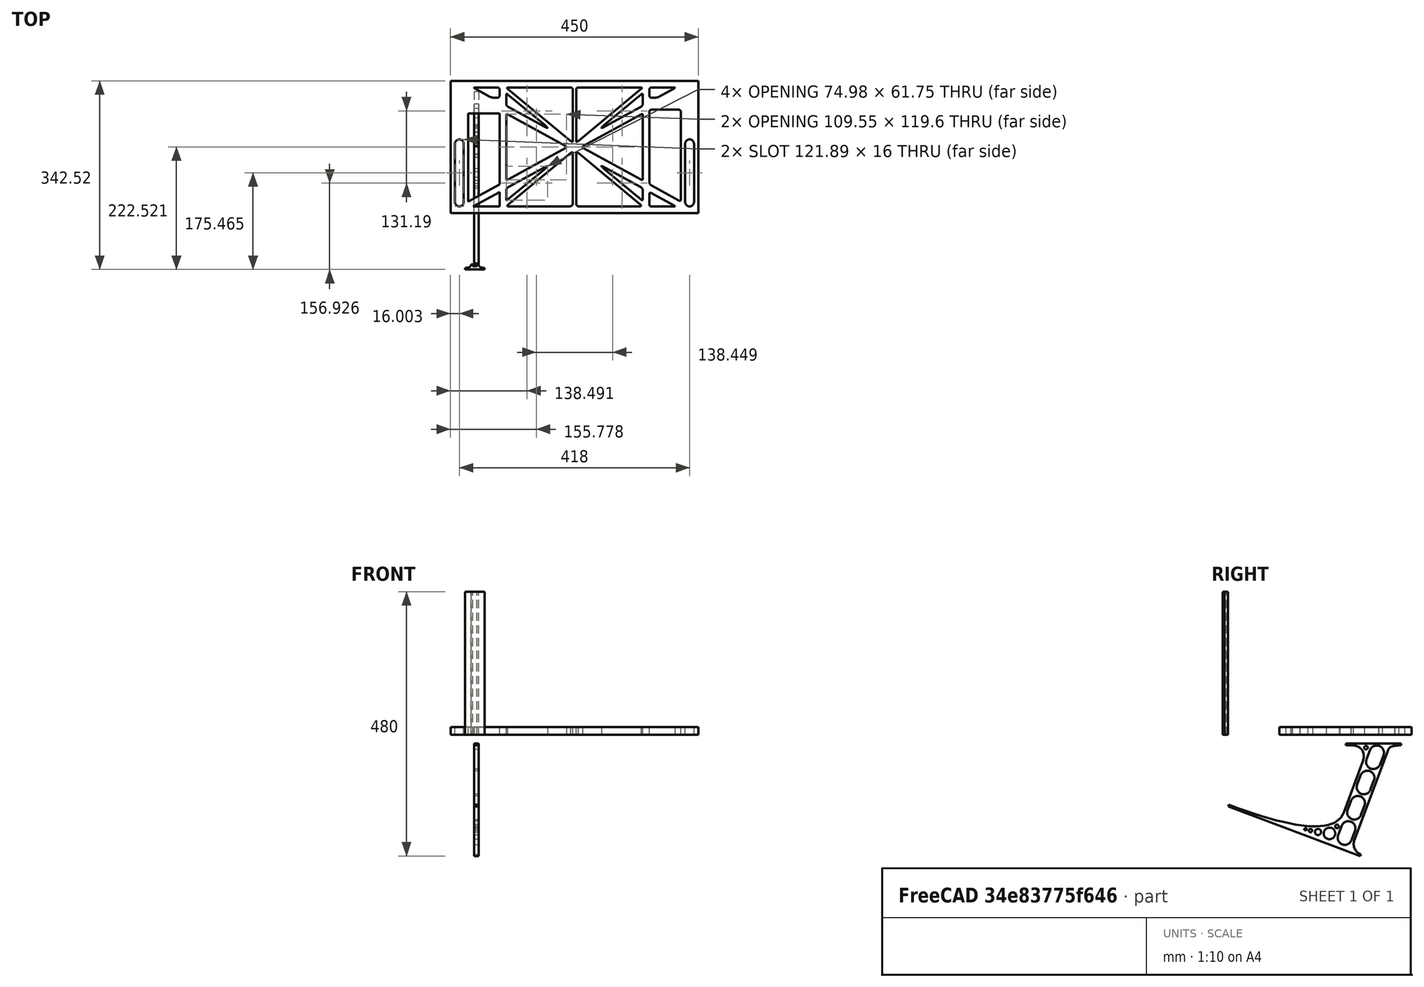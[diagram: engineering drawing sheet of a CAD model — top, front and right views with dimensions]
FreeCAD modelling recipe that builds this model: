
FCSTD DOCUMENT  (FreeCAD 0.19R0.19.2)
Label: laptopStand124FCStd
License: All rights reserved
LicenseURL: http://en.wikipedia.org/wiki/All_rights_reserved
objects: Sketcher::SketchObject×3, Part::Extrusion×3
note: 6 computed .brp shape members not serialized (recipe doc carries the construction recipe); baked Part::Feature solids carry a one-line shape summary decoded from their .brp

FEATURE [Sketcher::SketchObject] Sketch
  FullyConstrained = true
  sketch-geometry (348):
    g0: LineSegment StartX=-10.9272 StartY=-82.7794 StartZ=0 EndX=46.0728 EndY=-51.4823 EndZ=0
    g1: LineSegment StartX=-10.9272 StartY=77.3346 StartZ=0 EndX=-10.9272 EndY=-82.7794 EndZ=0
    g2: LineSegment StartX=46.0728 StartY=77.3346 StartZ=0 EndX=46.0728 EndY=-51.4823 EndZ=0
    g3: LineSegment StartX=-42.9272 StartY=136.221 StartZ=0 EndX=-42.9272 EndY=-103.779 EndZ=0
    g4: LineSegment StartX=407.073 StartY=136.221 StartZ=0 EndX=407.073 EndY=-103.779 EndZ=0
    g5: ArcOfCircle CenterX=-26.9272 CenterY=22.1087 CenterZ=0 NormalX=0 NormalY=0 NormalZ=1 AngleXU=0 Radius=8 StartAngle=1e-16 EndAngle=3.14159
    g6: ArcOfCircle CenterX=-26.9272 CenterY=-83.7794 CenterZ=0 NormalX=0 NormalY=0 NormalZ=1 AngleXU=0 Radius=8 StartAngle=3.14159 EndAngle=6.28319
    g7: LineSegment StartX=-34.9272 StartY=22.1087 StartZ=0 EndX=-34.9272 EndY=-83.7794 EndZ=0
    g8: LineSegment StartX=-18.9272 StartY=22.1087 StartZ=0 EndX=-18.9272 EndY=-83.7794 EndZ=0
    g9: ArcOfCircle CenterX=391.073 CenterY=22.1087 CenterZ=0 NormalX=0 NormalY=0 NormalZ=1 AngleXU=0 Radius=8 StartAngle=-4.4e-15 EndAngle=3.14159
    g10: LineSegment StartX=399.073 StartY=22.1087 StartZ=0 EndX=399.073 EndY=-83.7794 EndZ=0
    g11: LineSegment StartX=383.073 StartY=22.1087 StartZ=0 EndX=383.073 EndY=-83.7794 EndZ=0
    g12: ArcOfCircle CenterX=391.073 CenterY=-83.7794 CenterZ=0 NormalX=0 NormalY=0 NormalZ=1 AngleXU=0 Radius=8 StartAngle=3.14159 EndAngle=6.28319
    g13: Circle CenterX=175.022 CenterY=27.0628 CenterZ=0 NormalX=0 NormalY=0 NormalZ=1 AngleXU=0 Radius=1
    g14: Circle CenterX=179.022 CenterY=24.8665 CenterZ=0 NormalX=0 NormalY=0 NormalZ=1 AngleXU=0 Radius=1
    g15: Circle CenterX=179.022 CenterY=27.0628 CenterZ=0 NormalX=0 NormalY=0 NormalZ=1 AngleXU=0 Radius=1
    g16: BSplineCurve PolesCount=3 KnotsCount=2 Degree=2 IsPeriodic=0
    g17: GeomPoint X=175.022 Y=27.0628 Z=0
    g18: GeomPoint X=179.022 Y=27.0628 Z=0
    g19: Circle CenterX=189.124 CenterY=27.0628 CenterZ=0 NormalX=0 NormalY=0 NormalZ=1 AngleXU=0 Radius=1
    g20: Circle CenterX=185.124 CenterY=24.8665 CenterZ=0 NormalX=0 NormalY=0 NormalZ=1 AngleXU=0 Radius=1
    g21: Circle CenterX=185.124 CenterY=27.0628 CenterZ=0 NormalX=0 NormalY=0 NormalZ=1 AngleXU=0 Radius=1
    g22: BSplineCurve PolesCount=3 KnotsCount=2 Degree=2 IsPeriodic=0
    g23: GeomPoint X=189.124 Y=27.0628 Z=0
    g24: GeomPoint X=185.124 Y=27.0628 Z=0
    g25: Circle CenterX=175.022 CenterY=5.37834 CenterZ=0 NormalX=0 NormalY=0 NormalZ=1 AngleXU=0 Radius=1
    g26: Circle CenterX=179.022 CenterY=7.57463 CenterZ=0 NormalX=0 NormalY=0 NormalZ=1 AngleXU=0 Radius=1
    g27: Circle CenterX=179.022 CenterY=5.34704 CenterZ=0 NormalX=0 NormalY=0 NormalZ=1 AngleXU=0 Radius=1
    g28: BSplineCurve PolesCount=3 KnotsCount=2 Degree=2 IsPeriodic=0
    g29: GeomPoint X=175.022 Y=5.37834 Z=0
    g30: GeomPoint X=179.022 Y=5.34704 Z=0
    g31: Circle CenterX=189.124 CenterY=5.37834 CenterZ=0 NormalX=0 NormalY=0 NormalZ=1 AngleXU=0 Radius=1
    g32: Circle CenterX=185.124 CenterY=7.57463 CenterZ=0 NormalX=0 NormalY=0 NormalZ=1 AngleXU=0 Radius=1
    g33: Circle CenterX=185.124 CenterY=5.34704 CenterZ=0 NormalX=0 NormalY=0 NormalZ=1 AngleXU=0 Radius=1
    g34: BSplineCurve PolesCount=3 KnotsCount=2 Degree=2 IsPeriodic=0
    g35: GeomPoint X=189.124 Y=5.37834 Z=0
    g36: GeomPoint X=185.124 Y=5.34704 Z=0
    g37: Circle CenterX=165.871 CenterY=18.1458 CenterZ=0 NormalX=0 NormalY=0 NormalZ=1 AngleXU=0 Radius=1
    g38: Circle CenterX=169.377 CenterY=16.2206 CenterZ=0 NormalX=0 NormalY=0 NormalZ=1 AngleXU=0 Radius=1
    g39: Circle CenterX=165.871 CenterY=14.2954 CenterZ=0 NormalX=0 NormalY=0 NormalZ=1 AngleXU=0 Radius=1
    g40: BSplineCurve PolesCount=3 KnotsCount=2 Degree=2 IsPeriodic=0
    g41: GeomPoint X=165.871 Y=18.1458 Z=0
    g42: GeomPoint X=165.871 Y=14.2954 Z=0
    g43: Circle CenterX=198.275 CenterY=18.1458 CenterZ=0 NormalX=0 NormalY=0 NormalZ=1 AngleXU=0 Radius=1
    g44: Circle CenterX=194.768 CenterY=16.2206 CenterZ=0 NormalX=0 NormalY=0 NormalZ=1 AngleXU=0 Radius=1
    g45: Circle CenterX=198.275 CenterY=14.2954 CenterZ=0 NormalX=0 NormalY=0 NormalZ=1 AngleXU=0 Radius=1
    g46: BSplineCurve PolesCount=3 KnotsCount=2 Degree=2 IsPeriodic=0
    g47: GeomPoint X=198.275 Y=18.1458 Z=0
    g48: GeomPoint X=198.275 Y=14.2954 Z=0
    g49: LineSegment StartX=407.073 StartY=-103.779 StartZ=0 EndX=-42.9272 EndY=-103.779 EndZ=0
    g50: LineSegment StartX=407.073 StartY=136.221 StartZ=0 EndX=-42.9272 EndY=136.221 EndZ=0
    g51: LineSegment StartX=46.0728 StartY=77.3346 StartZ=0 EndX=-10.9272 EndY=77.3346 EndZ=0
    g52: Circle CenterX=125.607 CenterY=54.1951 CenterZ=0 NormalX=0 NormalY=0 NormalZ=1 AngleXU=0 Radius=1
    g53: Circle CenterX=139.632 CenterY=46.4944 CenterZ=0 NormalX=0 NormalY=0 NormalZ=1 AngleXU=0 Radius=1
    g54: Circle CenterX=127.326 CenterY=56.7187 CenterZ=0 NormalX=0 NormalY=0 NormalZ=1 AngleXU=0 Radius=1
    g55: BSplineCurve PolesCount=3 KnotsCount=2 Degree=2 IsPeriodic=0
    g56: GeomPoint X=125.607 Y=54.1951 Z=0
    g57: GeomPoint X=127.326 Y=56.7187 Z=0
    g58: Circle CenterX=236.821 CenterY=56.7187 CenterZ=0 NormalX=0 NormalY=0 NormalZ=1 AngleXU=0 Radius=1
    g59: Circle CenterX=224.513 CenterY=46.4944 CenterZ=0 NormalX=0 NormalY=0 NormalZ=1 AngleXU=0 Radius=1
    g60: Circle CenterX=238.538 CenterY=54.1951 CenterZ=0 NormalX=0 NormalY=0 NormalZ=1 AngleXU=0 Radius=1
    g61: BSplineCurve PolesCount=3 KnotsCount=2 Degree=2 IsPeriodic=0
    g62: GeomPoint X=236.821 Y=56.7187 Z=0
    g63: GeomPoint X=238.538 Y=54.1951 Z=0
    g64: Circle CenterX=238.538 CenterY=-21.7539 CenterZ=0 NormalX=0 NormalY=0 NormalZ=1 AngleXU=0 Radius=1
    g65: Circle CenterX=224.513 CenterY=-14.0532 CenterZ=0 NormalX=0 NormalY=0 NormalZ=1 AngleXU=0 Radius=1
    g66: Circle CenterX=236.821 CenterY=-24.2775 CenterZ=0 NormalX=0 NormalY=0 NormalZ=1 AngleXU=0 Radius=1
    g67: BSplineCurve PolesCount=3 KnotsCount=2 Degree=2 IsPeriodic=0
    g68: GeomPoint X=238.538 Y=-21.7539 Z=0
    g69: GeomPoint X=236.821 Y=-24.2775 Z=0
    g70: Circle CenterX=125.607 CenterY=-21.7539 CenterZ=0 NormalX=0 NormalY=0 NormalZ=1 AngleXU=0 Radius=1
    g71: Circle CenterX=139.632 CenterY=-14.0532 CenterZ=0 NormalX=0 NormalY=0 NormalZ=1 AngleXU=0 Radius=1
    g72: Circle CenterX=127.325 CenterY=-24.2775 CenterZ=0 NormalX=0 NormalY=0 NormalZ=1 AngleXU=0 Radius=1
    g73: BSplineCurve PolesCount=3 KnotsCount=2 Degree=2 IsPeriodic=0
    g74: GeomPoint X=125.607 Y=-21.7539 Z=0
    g75: GeomPoint X=127.325 Y=-24.2775 Z=0
    g76: Circle CenterX=302.996 CenterY=111.695 CenterZ=0 NormalX=0 NormalY=0 NormalZ=1 AngleXU=0 Radius=1
    g77: Circle CenterX=306.073 CenterY=114.251 CenterZ=0 NormalX=0 NormalY=0 NormalZ=1 AngleXU=0 Radius=1
    g78: Circle CenterX=306.073 CenterY=110.251 CenterZ=0 NormalX=0 NormalY=0 NormalZ=1 AngleXU=0 Radius=1
    g79: BSplineCurve PolesCount=3 KnotsCount=2 Degree=2 IsPeriodic=0
    g80: GeomPoint X=302.996 Y=111.695 Z=0
    g81: GeomPoint X=306.073 Y=110.251 Z=0
    g82: Circle CenterX=306.073 CenterY=95.2763 CenterZ=0 NormalX=0 NormalY=0 NormalZ=1 AngleXU=0 Radius=1
    g83: Circle CenterX=306.073 CenterY=91.2763 CenterZ=0 NormalX=0 NormalY=0 NormalZ=1 AngleXU=0 Radius=1
    g84: Circle CenterX=302.567 CenterY=89.3511 CenterZ=0 NormalX=0 NormalY=0 NormalZ=1 AngleXU=0 Radius=1
    g85: BSplineCurve PolesCount=3 KnotsCount=2 Degree=2 IsPeriodic=0
    g86: GeomPoint X=306.073 Y=95.2763 Z=0
    g87: GeomPoint X=302.567 Y=89.3511 Z=0
    g88: LineSegment StartX=306.073 StartY=110.251 StartZ=0 EndX=306.073 EndY=95.2763 EndZ=0
    g89: LineSegment StartX=302.996 StartY=111.695 StartZ=0 EndX=236.821 EndY=56.7187 EndZ=0
    g90: LineSegment StartX=238.538 StartY=54.1951 StartZ=0 EndX=302.567 EndY=89.3511 EndZ=0
    g91: Circle CenterX=61.1496 CenterY=111.695 CenterZ=0 NormalX=0 NormalY=0 NormalZ=1 AngleXU=0 Radius=1
    g92: Circle CenterX=58.0728 CenterY=114.251 CenterZ=0 NormalX=0 NormalY=0 NormalZ=1 AngleXU=0 Radius=1
    g93: Circle CenterX=58.0728 CenterY=110.251 CenterZ=0 NormalX=0 NormalY=0 NormalZ=1 AngleXU=0 Radius=1
    g94: BSplineCurve PolesCount=3 KnotsCount=2 Degree=2 IsPeriodic=0
    g95: GeomPoint X=61.1496 Y=111.695 Z=0
    g96: GeomPoint X=58.0728 Y=110.251 Z=0
    g97: Circle CenterX=61.5791 CenterY=89.3511 CenterZ=0 NormalX=0 NormalY=0 NormalZ=1 AngleXU=0 Radius=1
    g98: Circle CenterX=58.0728 CenterY=91.2763 CenterZ=0 NormalX=0 NormalY=0 NormalZ=1 AngleXU=0 Radius=1
    g99: Circle CenterX=58.0728 CenterY=95.2763 CenterZ=0 NormalX=0 NormalY=0 NormalZ=1 AngleXU=0 Radius=1
    g100: BSplineCurve PolesCount=3 KnotsCount=2 Degree=2 IsPeriodic=0
    g101: GeomPoint X=61.5791 Y=89.3511 Z=0
    g102: GeomPoint X=58.0728 Y=95.2763 Z=0
    g103: LineSegment StartX=58.0728 StartY=110.251 StartZ=0 EndX=58.0728 EndY=95.2763 EndZ=0
    g104: LineSegment StartX=61.1496 StartY=111.695 StartZ=0 EndX=127.326 EndY=56.7187 EndZ=0
    g105: LineSegment StartX=125.607 StartY=54.1951 StartZ=0 EndX=61.5791 EndY=89.3511 EndZ=0
    g106: Circle CenterX=61.5791 CenterY=-56.9099 CenterZ=0 NormalX=0 NormalY=0 NormalZ=1 AngleXU=0 Radius=1
    g107: Circle CenterX=58.0728 CenterY=-58.8351 CenterZ=0 NormalX=0 NormalY=0 NormalZ=1 AngleXU=0 Radius=1
    g108: Circle CenterX=58.0728 CenterY=-62.8351 CenterZ=0 NormalX=0 NormalY=0 NormalZ=1 AngleXU=0 Radius=1
    g109: BSplineCurve PolesCount=3 KnotsCount=2 Degree=2 IsPeriodic=0
    g110: GeomPoint X=61.5791 Y=-56.9099 Z=0
    g111: GeomPoint X=58.0728 Y=-62.8351 Z=0
    g112: Circle CenterX=58.0728 CenterY=-77.8102 CenterZ=0 NormalX=0 NormalY=0 NormalZ=1 AngleXU=0 Radius=1
    g113: Circle CenterX=58.0728 CenterY=-81.8102 CenterZ=0 NormalX=0 NormalY=0 NormalZ=1 AngleXU=0 Radius=1
    g114: Circle CenterX=61.1496 CenterY=-79.2541 CenterZ=0 NormalX=0 NormalY=0 NormalZ=1 AngleXU=0 Radius=1
    g115: BSplineCurve PolesCount=3 KnotsCount=2 Degree=2 IsPeriodic=0
    g116: GeomPoint X=58.0728 Y=-77.8102 Z=0
    g117: GeomPoint X=61.1496 Y=-79.2541 Z=0
    g118: LineSegment StartX=58.0728 StartY=-62.8351 StartZ=0 EndX=58.0728 EndY=-77.8102 EndZ=0
    g119: LineSegment StartX=61.1496 StartY=-79.2541 StartZ=0 EndX=127.325 EndY=-24.2775 EndZ=0
    g120: LineSegment StartX=125.607 StartY=-21.7539 StartZ=0 EndX=61.5791 EndY=-56.9099 EndZ=0
    g121: Circle CenterX=302.567 CenterY=-56.9099 CenterZ=0 NormalX=0 NormalY=0 NormalZ=1 AngleXU=0 Radius=1
    g122: Circle CenterX=306.073 CenterY=-58.8351 CenterZ=0 NormalX=0 NormalY=0 NormalZ=1 AngleXU=0 Radius=1
    g123: Circle CenterX=306.073 CenterY=-62.8351 CenterZ=0 NormalX=0 NormalY=0 NormalZ=1 AngleXU=0 Radius=1
    g124: BSplineCurve PolesCount=3 KnotsCount=2 Degree=2 IsPeriodic=0
    g125: GeomPoint X=302.567 Y=-56.9099 Z=0
    g126: GeomPoint X=306.073 Y=-62.8351 Z=0
    g127: Circle CenterX=302.996 CenterY=-79.2541 CenterZ=0 NormalX=0 NormalY=0 NormalZ=1 AngleXU=0 Radius=1
    g128: Circle CenterX=306.073 CenterY=-81.8102 CenterZ=0 NormalX=0 NormalY=0 NormalZ=1 AngleXU=0 Radius=1
    g129: Circle CenterX=306.073 CenterY=-77.8102 CenterZ=0 NormalX=0 NormalY=0 NormalZ=1 AngleXU=0 Radius=1
    g130: BSplineCurve PolesCount=3 KnotsCount=2 Degree=2 IsPeriodic=0
    g131: GeomPoint X=302.996 Y=-79.2541 Z=0
    g132: GeomPoint X=306.073 Y=-77.8102 Z=0
    g133: LineSegment StartX=306.073 StartY=-62.8351 StartZ=0 EndX=306.073 EndY=-77.8102 EndZ=0
    g134: LineSegment StartX=302.996 StartY=-79.2541 StartZ=0 EndX=236.821 EndY=-24.2775 EndZ=0
    g135: LineSegment StartX=238.538 StartY=-21.7539 StartZ=0 EndX=302.567 EndY=-56.9099 EndZ=0
    g136: Circle CenterX=61.6457 CenterY=-88.8112 CenterZ=0 NormalX=0 NormalY=0 NormalZ=1 AngleXU=0 Radius=1
    g137: Circle CenterX=58.0728 CenterY=-91.7794 CenterZ=0 NormalX=0 NormalY=0 NormalZ=1 AngleXU=0 Radius=1
    g138: Circle CenterX=63.9135 CenterY=-91.7794 CenterZ=0 NormalX=0 NormalY=0 NormalZ=1 AngleXU=0 Radius=1
    g139: BSplineCurve PolesCount=3 KnotsCount=2 Degree=2 IsPeriodic=0
    g140: GeomPoint X=61.6457 Y=-88.8112 Z=0
    g141: GeomPoint X=63.9135 Y=-91.7794 Z=0
    g142: Circle CenterX=179.022 CenterY=-85.8163 CenterZ=0 NormalX=0 NormalY=0 NormalZ=1 AngleXU=0 Radius=1
    g143: Circle CenterX=179.022 CenterY=-91.7794 CenterZ=0 NormalX=0 NormalY=0 NormalZ=1 AngleXU=0 Radius=1
    g144: Circle CenterX=171.895 CenterY=-91.7794 CenterZ=0 NormalX=0 NormalY=0 NormalZ=1 AngleXU=0 Radius=1
    g145: BSplineCurve PolesCount=3 KnotsCount=2 Degree=2 IsPeriodic=0
    g146: GeomPoint X=179.022 Y=-85.8163 Z=0
    g147: GeomPoint X=171.895 Y=-91.7794 Z=0
    g148: Circle CenterX=185.124 CenterY=-86.2028 CenterZ=0 NormalX=0 NormalY=0 NormalZ=1 AngleXU=0 Radius=1
    g149: Circle CenterX=185.124 CenterY=-91.7794 CenterZ=0 NormalX=0 NormalY=0 NormalZ=1 AngleXU=0 Radius=1
    g150: Circle CenterX=191.747 CenterY=-91.7794 CenterZ=0 NormalX=0 NormalY=0 NormalZ=1 AngleXU=0 Radius=1
    g151: BSplineCurve PolesCount=3 KnotsCount=2 Degree=2 IsPeriodic=0
    g152: GeomPoint X=185.124 Y=-86.2028 Z=0
    g153: GeomPoint X=191.747 Y=-91.7794 Z=0
    g154: Circle CenterX=299.888 CenterY=-86.6413 CenterZ=0 NormalX=0 NormalY=0 NormalZ=1 AngleXU=0 Radius=1
    g155: Circle CenterX=306.073 CenterY=-91.7794 CenterZ=0 NormalX=0 NormalY=0 NormalZ=1 AngleXU=0 Radius=1
    g156: Circle CenterX=298.776 CenterY=-91.7794 CenterZ=0 NormalX=0 NormalY=0 NormalZ=1 AngleXU=0 Radius=1
    g157: BSplineCurve PolesCount=3 KnotsCount=2 Degree=2 IsPeriodic=0
    g158: GeomPoint X=299.888 Y=-86.6413 Z=0
    g159: GeomPoint X=298.776 Y=-91.7794 Z=0
    g160: LineSegment StartX=189.124 StartY=5.37834 StartZ=0 EndX=299.888 EndY=-86.6413 EndZ=0
    g161: LineSegment StartX=298.776 StartY=-91.7794 StartZ=0 EndX=191.747 EndY=-91.7794 EndZ=0
    g162: LineSegment StartX=185.124 StartY=-86.2028 StartZ=0 EndX=185.124 EndY=5.34704 EndZ=0
    g163: LineSegment StartX=179.022 StartY=5.34704 StartZ=0 EndX=179.022 EndY=-85.8163 EndZ=0
    g164: LineSegment StartX=171.895 StartY=-91.7794 StartZ=0 EndX=63.9135 EndY=-91.7794 EndZ=0
    g165: LineSegment StartX=61.6457 StartY=-88.8112 StartZ=0 EndX=175.022 EndY=5.37834 EndZ=0
    g166: Circle CenterX=302.073 CenterY=124.221 CenterZ=0 NormalX=0 NormalY=0 NormalZ=1 AngleXU=0 Radius=1
    g167: Circle CenterX=306.073 CenterY=124.221 CenterZ=0 NormalX=0 NormalY=0 NormalZ=1 AngleXU=0 Radius=1
    g168: Circle CenterX=302.996 CenterY=121.665 CenterZ=0 NormalX=0 NormalY=0 NormalZ=1 AngleXU=0 Radius=1
    g169: BSplineCurve PolesCount=3 KnotsCount=2 Degree=2 IsPeriodic=0
    g170: GeomPoint X=302.073 Y=124.221 Z=0
    g171: GeomPoint X=302.996 Y=121.665 Z=0
    g172: Circle CenterX=189.124 CenterY=124.221 CenterZ=0 NormalX=0 NormalY=0 NormalZ=1 AngleXU=0 Radius=1
    g173: Circle CenterX=185.124 CenterY=124.221 CenterZ=0 NormalX=0 NormalY=0 NormalZ=1 AngleXU=0 Radius=1
    g174: Circle CenterX=185.124 CenterY=120.221 CenterZ=0 NormalX=0 NormalY=0 NormalZ=1 AngleXU=0 Radius=1
    g175: BSplineCurve PolesCount=3 KnotsCount=2 Degree=2 IsPeriodic=0
    g176: GeomPoint X=189.124 Y=124.221 Z=0
    g177: GeomPoint X=185.124 Y=120.221 Z=0
    g178: Circle CenterX=175.022 CenterY=124.221 CenterZ=0 NormalX=0 NormalY=0 NormalZ=1 AngleXU=0 Radius=1
    g179: Circle CenterX=179.022 CenterY=124.221 CenterZ=0 NormalX=0 NormalY=0 NormalZ=1 AngleXU=0 Radius=1
    g180: Circle CenterX=179.022 CenterY=120.221 CenterZ=0 NormalX=0 NormalY=0 NormalZ=1 AngleXU=0 Radius=1
    g181: BSplineCurve PolesCount=3 KnotsCount=2 Degree=2 IsPeriodic=0
    g182: GeomPoint X=175.022 Y=124.221 Z=0
    g183: GeomPoint X=179.022 Y=120.221 Z=0
    g184: Circle CenterX=62.0728 CenterY=124.221 CenterZ=0 NormalX=0 NormalY=0 NormalZ=1 AngleXU=0 Radius=1
    g185: Circle CenterX=58.0728 CenterY=124.221 CenterZ=0 NormalX=0 NormalY=0 NormalZ=1 AngleXU=0 Radius=1
    g186: Circle CenterX=61.1496 CenterY=121.665 CenterZ=0 NormalX=0 NormalY=0 NormalZ=1 AngleXU=0 Radius=1
    g187: BSplineCurve PolesCount=3 KnotsCount=2 Degree=2 IsPeriodic=0
    g188: GeomPoint X=62.0728 Y=124.221 Z=0
    g189: GeomPoint X=61.1496 Y=121.665 Z=0
    g190: LineSegment StartX=62.0728 StartY=124.221 StartZ=0 EndX=175.022 EndY=124.221 EndZ=0
    g191: LineSegment StartX=179.022 StartY=120.221 StartZ=0 EndX=179.022 EndY=27.0628 EndZ=0
    g192: LineSegment StartX=185.124 StartY=27.0628 StartZ=0 EndX=185.124 EndY=120.221 EndZ=0
    g193: LineSegment StartX=189.124 StartY=124.221 StartZ=0 EndX=302.073 EndY=124.221 EndZ=0
    g194: LineSegment StartX=302.996 StartY=121.665 StartZ=0 EndX=189.124 EndY=27.0628 EndZ=0
    g195: LineSegment StartX=175.022 StartY=27.0628 StartZ=0 EndX=61.1496 EndY=121.665 EndZ=0
    g196: Circle CenterX=61.5791 CenterY=75.4095 CenterZ=0 NormalX=0 NormalY=0 NormalZ=1 AngleXU=0 Radius=1
    g197: Circle CenterX=58.0728 CenterY=77.3346 CenterZ=0 NormalX=0 NormalY=0 NormalZ=1 AngleXU=0 Radius=1
    g198: Circle CenterX=58.0728 CenterY=73.3346 CenterZ=0 NormalX=0 NormalY=0 NormalZ=1 AngleXU=0 Radius=1
    g199: BSplineCurve PolesCount=3 KnotsCount=2 Degree=2 IsPeriodic=0
    g200: GeomPoint X=61.5791 Y=75.4095 Z=0
    g201: GeomPoint X=58.0728 Y=73.3346 Z=0
    g202: Circle CenterX=58.0728 CenterY=-40.8935 CenterZ=0 NormalX=0 NormalY=0 NormalZ=1 AngleXU=0 Radius=1
    g203: Circle CenterX=58.0728 CenterY=-44.8935 CenterZ=0 NormalX=0 NormalY=0 NormalZ=1 AngleXU=0 Radius=1
    g204: Circle CenterX=61.5791 CenterY=-42.9683 CenterZ=0 NormalX=0 NormalY=0 NormalZ=1 AngleXU=0 Radius=1
    g205: BSplineCurve PolesCount=3 KnotsCount=2 Degree=2 IsPeriodic=0
    g206: GeomPoint X=58.0728 Y=-40.8935 Z=0
    g207: GeomPoint X=61.5791 Y=-42.9683 Z=0
    g208: LineSegment StartX=61.5791 StartY=-42.9683 StartZ=0 EndX=165.871 EndY=14.2954 EndZ=0
    g209: LineSegment StartX=165.871 StartY=18.1458 StartZ=0 EndX=61.5791 EndY=75.4095 EndZ=0
    g210: LineSegment StartX=58.0728 StartY=73.3346 StartZ=0 EndX=58.0728 EndY=-40.8935 EndZ=0
    g211: Circle CenterX=302.567 CenterY=-42.9683 CenterZ=0 NormalX=0 NormalY=0 NormalZ=1 AngleXU=0 Radius=1
    g212: Circle CenterX=306.073 CenterY=-44.8935 CenterZ=0 NormalX=0 NormalY=0 NormalZ=1 AngleXU=0 Radius=1
    g213: Circle CenterX=306.073 CenterY=-40.8935 CenterZ=0 NormalX=0 NormalY=0 NormalZ=1 AngleXU=0 Radius=1
    g214: BSplineCurve PolesCount=3 KnotsCount=2 Degree=2 IsPeriodic=0
    g215: GeomPoint X=302.567 Y=-42.9683 Z=0
    g216: GeomPoint X=306.073 Y=-40.8935 Z=0
    g217: Circle CenterX=306.073 CenterY=73.3346 CenterZ=0 NormalX=0 NormalY=0 NormalZ=1 AngleXU=0 Radius=1
    g218: Circle CenterX=306.073 CenterY=77.3346 CenterZ=0 NormalX=0 NormalY=0 NormalZ=1 AngleXU=0 Radius=1
    g219: Circle CenterX=302.567 CenterY=75.4095 CenterZ=0 NormalX=0 NormalY=0 NormalZ=1 AngleXU=0 Radius=1
    g220: BSplineCurve PolesCount=3 KnotsCount=2 Degree=2 IsPeriodic=0
    g221: GeomPoint X=306.073 Y=73.3346 Z=0
    g222: GeomPoint X=302.567 Y=75.4095 Z=0
    g223: LineSegment StartX=302.567 StartY=-42.9683 StartZ=0 EndX=198.275 EndY=14.2954 EndZ=0
    g224: LineSegment StartX=198.275 StartY=18.1458 StartZ=0 EndX=302.567 EndY=75.4095 EndZ=0
    g225: LineSegment StartX=306.073 StartY=73.3346 StartZ=0 EndX=306.073 EndY=-40.8935 EndZ=0
    g226: LineSegment StartX=322.073 StartY=105.865 StartZ=0 EndX=328.643 EndY=105.865 EndZ=0
    g227: LineSegment StartX=318.073 StartY=120.221 StartZ=0 EndX=318.073 EndY=109.865 EndZ=0
    g228: LineSegment StartX=336.157 StartY=107.779 StartZ=0 EndX=362.567 EndY=122.294 EndZ=0
    g229: Circle CenterX=362.073 CenterY=124.221 CenterZ=0 NormalX=0 NormalY=0 NormalZ=1 AngleXU=0 Radius=1
    g230: Circle CenterX=366.073 CenterY=124.221 CenterZ=0 NormalX=0 NormalY=0 NormalZ=1 AngleXU=0 Radius=1
    g231: Circle CenterX=362.567 CenterY=122.294 CenterZ=0 NormalX=0 NormalY=0 NormalZ=1 AngleXU=0 Radius=1
    g232: BSplineCurve PolesCount=3 KnotsCount=2 Degree=2 IsPeriodic=0
    g233: GeomPoint X=362.073 Y=124.221 Z=0
    g234: GeomPoint X=362.567 Y=122.294 Z=0
    g235: Circle CenterX=322.073 CenterY=124.221 CenterZ=0 NormalX=0 NormalY=0 NormalZ=1 AngleXU=0 Radius=1
    g236: Circle CenterX=318.073 CenterY=124.221 CenterZ=0 NormalX=0 NormalY=0 NormalZ=1 AngleXU=0 Radius=1
    g237: Circle CenterX=318.073 CenterY=120.221 CenterZ=0 NormalX=0 NormalY=0 NormalZ=1 AngleXU=0 Radius=1
    g238: BSplineCurve PolesCount=3 KnotsCount=2 Degree=2 IsPeriodic=0
    g239: GeomPoint X=322.073 Y=124.221 Z=0
    g240: GeomPoint X=318.073 Y=120.221 Z=0
    g241: Circle CenterX=322.073 CenterY=105.865 CenterZ=0 NormalX=0 NormalY=0 NormalZ=1 AngleXU=0 Radius=1
    g242: Circle CenterX=318.073 CenterY=105.865 CenterZ=0 NormalX=0 NormalY=0 NormalZ=1 AngleXU=0 Radius=1
    g243: Circle CenterX=318.073 CenterY=109.865 CenterZ=0 NormalX=0 NormalY=0 NormalZ=1 AngleXU=0 Radius=1
    g244: BSplineCurve PolesCount=3 KnotsCount=2 Degree=2 IsPeriodic=0
    g245: GeomPoint X=322.073 Y=105.865 Z=0
    g246: GeomPoint X=318.073 Y=109.865 Z=0
    g247: Circle CenterX=336.157 CenterY=107.779 CenterZ=0 NormalX=0 NormalY=0 NormalZ=1 AngleXU=0 Radius=1
    g248: Circle CenterX=332.651 CenterY=105.853 CenterZ=0 NormalX=0 NormalY=0 NormalZ=1 AngleXU=0 Radius=1
    g249: Circle CenterX=328.643 CenterY=105.865 CenterZ=0 NormalX=0 NormalY=0 NormalZ=1 AngleXU=0 Radius=1
    g250: BSplineCurve PolesCount=3 KnotsCount=2 Degree=2 IsPeriodic=0
    g251: GeomPoint X=336.157 Y=107.779 Z=0
    g252: GeomPoint X=328.643 Y=105.865 Z=0
    g253: LineSegment StartX=322.073 StartY=124.221 StartZ=0 EndX=362.073 EndY=124.221 EndZ=0
    g254: Circle CenterX=371.567 CenterY=-80.8644 CenterZ=0 NormalX=0 NormalY=0 NormalZ=1 AngleXU=0 Radius=1
    g255: Circle CenterX=375.073 CenterY=-82.7896 CenterZ=0 NormalX=0 NormalY=0 NormalZ=1 AngleXU=0 Radius=1
    g256: Circle CenterX=375.073 CenterY=-78.7896 CenterZ=0 NormalX=0 NormalY=0 NormalZ=1 AngleXU=0 Radius=1
    g257: BSplineCurve PolesCount=3 KnotsCount=2 Degree=2 IsPeriodic=0
    g258: GeomPoint X=371.567 Y=-80.8644 Z=0
    g259: GeomPoint X=375.073 Y=-78.7896 Z=0
    g260: Circle CenterX=321.579 CenterY=-53.4075 CenterZ=0 NormalX=0 NormalY=0 NormalZ=1 AngleXU=0 Radius=1
    g261: Circle CenterX=318.073 CenterY=-51.4823 CenterZ=0 NormalX=0 NormalY=0 NormalZ=1 AngleXU=0 Radius=1
    g262: Circle CenterX=318.073 CenterY=-47.4823 CenterZ=0 NormalX=0 NormalY=0 NormalZ=1 AngleXU=0 Radius=1
    g263: BSplineCurve PolesCount=3 KnotsCount=2 Degree=2 IsPeriodic=0
    g264: GeomPoint X=321.579 Y=-53.4075 Z=0
    g265: GeomPoint X=318.073 Y=-47.4823 Z=0
    g266: Circle CenterX=318.073 CenterY=79.9235 CenterZ=0 NormalX=0 NormalY=0 NormalZ=1 AngleXU=0 Radius=1
    g267: Circle CenterX=318.073 CenterY=83.9235 CenterZ=0 NormalX=0 NormalY=0 NormalZ=1 AngleXU=0 Radius=1
    g268: Circle CenterX=322.073 CenterY=83.9235 CenterZ=0 NormalX=0 NormalY=0 NormalZ=1 AngleXU=0 Radius=1
    g269: BSplineCurve PolesCount=3 KnotsCount=2 Degree=2 IsPeriodic=0
    g270: GeomPoint X=318.073 Y=79.9235 Z=0
    g271: GeomPoint X=322.073 Y=83.9235 Z=0
    g272: Circle CenterX=375.073 CenterY=79.9235 CenterZ=0 NormalX=0 NormalY=0 NormalZ=1 AngleXU=0 Radius=1
    g273: Circle CenterX=375.073 CenterY=83.9235 CenterZ=0 NormalX=0 NormalY=0 NormalZ=1 AngleXU=0 Radius=1
    g274: Circle CenterX=371.073 CenterY=83.9235 CenterZ=0 NormalX=0 NormalY=0 NormalZ=1 AngleXU=0 Radius=1
    g275: BSplineCurve PolesCount=3 KnotsCount=2 Degree=2 IsPeriodic=0
    g276: GeomPoint X=375.073 Y=79.9235 Z=0
    g277: GeomPoint X=371.073 Y=83.9235 Z=0
    g278: LineSegment StartX=322.073 StartY=83.9235 StartZ=0 EndX=371.073 EndY=83.9235 EndZ=0
    g279: LineSegment StartX=375.073 StartY=79.9235 StartZ=0 EndX=375.073 EndY=-78.7896 EndZ=0
    g280: LineSegment StartX=371.567 StartY=-80.8644 StartZ=0 EndX=321.579 EndY=-53.4075 EndZ=0
    g281: LineSegment StartX=318.073 StartY=-47.4823 StartZ=0 EndX=318.073 EndY=79.9235 EndZ=0
    g282: Circle CenterX=321.579 CenterY=-67.3492 CenterZ=0 NormalX=0 NormalY=0 NormalZ=1 AngleXU=0 Radius=1
    g283: Circle CenterX=318.073 CenterY=-65.424 CenterZ=0 NormalX=0 NormalY=0 NormalZ=1 AngleXU=0 Radius=1
    g284: Circle CenterX=318.073 CenterY=-69.424 CenterZ=0 NormalX=0 NormalY=0 NormalZ=1 AngleXU=0 Radius=1
    g285: BSplineCurve PolesCount=3 KnotsCount=2 Degree=2 IsPeriodic=0
    g286: GeomPoint X=321.579 Y=-67.3492 Z=0
    g287: GeomPoint X=318.073 Y=-69.424 Z=0
    g288: Circle CenterX=362.567 CenterY=-89.8542 CenterZ=0 NormalX=0 NormalY=0 NormalZ=1 AngleXU=0 Radius=1
    g289: Circle CenterX=366.073 CenterY=-91.7794 CenterZ=0 NormalX=0 NormalY=0 NormalZ=1 AngleXU=0 Radius=1
    g290: Circle CenterX=362.073 CenterY=-91.7794 CenterZ=0 NormalX=0 NormalY=0 NormalZ=1 AngleXU=0 Radius=1
    g291: BSplineCurve PolesCount=3 KnotsCount=2 Degree=2 IsPeriodic=0
    g292: GeomPoint X=362.567 Y=-89.8542 Z=0
    g293: GeomPoint X=362.073 Y=-91.7794 Z=0
    g294: Circle CenterX=322.073 CenterY=-91.7794 CenterZ=0 NormalX=0 NormalY=0 NormalZ=1 AngleXU=0 Radius=1
    g295: Circle CenterX=318.073 CenterY=-91.7794 CenterZ=0 NormalX=0 NormalY=0 NormalZ=1 AngleXU=0 Radius=1
    g296: Circle CenterX=318.073 CenterY=-87.7794 CenterZ=0 NormalX=0 NormalY=0 NormalZ=1 AngleXU=0 Radius=1
    g297: BSplineCurve PolesCount=3 KnotsCount=2 Degree=2 IsPeriodic=0
    g298: GeomPoint X=322.073 Y=-91.7794 Z=0
    g299: GeomPoint X=318.073 Y=-87.7794 Z=0
    g300: LineSegment StartX=362.567 StartY=-89.8542 StartZ=0 EndX=321.579 EndY=-67.3492 EndZ=0
    g301: LineSegment StartX=318.073 StartY=-69.424 StartZ=0 EndX=318.073 EndY=-87.7794 EndZ=0
    g302: LineSegment StartX=322.073 StartY=-91.7794 StartZ=0 EndX=362.073 EndY=-91.7794 EndZ=0
    g303: Circle CenterX=2.07281 CenterY=124.221 CenterZ=0 NormalX=0 NormalY=0 NormalZ=1 AngleXU=0 Radius=1
    g304: Circle CenterX=1.57905 CenterY=122.295 CenterZ=0 NormalX=0 NormalY=0 NormalZ=1 AngleXU=0 Radius=1
    g305: BSplineCurve PolesCount=3 KnotsCount=2 Degree=2 IsPeriodic=0
    g306: GeomPoint X=2.07281 Y=124.221 Z=0
    g307: GeomPoint X=1.57905 Y=122.295 Z=0
    g308: Circle CenterX=42.0728 CenterY=124.221 CenterZ=0 NormalX=0 NormalY=0 NormalZ=1 AngleXU=0 Radius=1
    g309: Circle CenterX=46.0728 CenterY=124.221 CenterZ=0 NormalX=0 NormalY=0 NormalZ=1 AngleXU=0 Radius=1
    g310: Circle CenterX=46.0728 CenterY=120.221 CenterZ=0 NormalX=0 NormalY=0 NormalZ=1 AngleXU=0 Radius=1
    g311: BSplineCurve PolesCount=3 KnotsCount=2 Degree=2 IsPeriodic=0
    g312: GeomPoint X=42.0728 Y=124.221 Z=0
    g313: GeomPoint X=46.0728 Y=120.221 Z=0
    g314: Circle CenterX=46.0728 CenterY=109.865 CenterZ=0 NormalX=0 NormalY=0 NormalZ=1 AngleXU=0 Radius=1
    g315: Circle CenterX=46.0728 CenterY=105.865 CenterZ=0 NormalX=0 NormalY=0 NormalZ=1 AngleXU=0 Radius=1
    g316: Circle CenterX=42.0728 CenterY=105.865 CenterZ=0 NormalX=0 NormalY=0 NormalZ=1 AngleXU=0 Radius=1
    g317: BSplineCurve PolesCount=3 KnotsCount=2 Degree=2 IsPeriodic=0
    g318: GeomPoint X=46.0728 Y=109.865 Z=0
    g319: GeomPoint X=42.0728 Y=105.865 Z=0
    g320: Circle CenterX=35.5028 CenterY=105.865 CenterZ=0 NormalX=0 NormalY=0 NormalZ=1 AngleXU=0 Radius=1
    g321: Circle CenterX=31.5028 CenterY=105.865 CenterZ=0 NormalX=0 NormalY=0 NormalZ=1 AngleXU=0 Radius=1
    g322: Circle CenterX=27.9965 CenterY=107.79 CenterZ=0 NormalX=0 NormalY=0 NormalZ=1 AngleXU=0 Radius=1
    g323: BSplineCurve PolesCount=3 KnotsCount=2 Degree=2 IsPeriodic=0
    g324: GeomPoint X=35.5028 Y=105.865 Z=0
    g325: GeomPoint X=27.9965 Y=107.79 Z=0
    g326: LineSegment StartX=2.07281 StartY=124.221 StartZ=0 EndX=42.0728 EndY=124.221 EndZ=0
    g327: LineSegment StartX=46.0728 StartY=120.221 StartZ=0 EndX=46.0728 EndY=109.865 EndZ=0
    g328: LineSegment StartX=42.0728 StartY=105.865 StartZ=0 EndX=35.5028 EndY=105.865 EndZ=0
    g329: LineSegment StartX=27.9965 StartY=107.79 StartZ=0 EndX=1.57905 EndY=122.295 EndZ=0
    g330: Circle CenterX=42.5666 CenterY=-67.3492 CenterZ=0 NormalX=0 NormalY=0 NormalZ=1 AngleXU=0 Radius=1
    g331: Circle CenterX=46.0728 CenterY=-65.424 CenterZ=0 NormalX=0 NormalY=0 NormalZ=1 AngleXU=0 Radius=1
    g332: Circle CenterX=46.0728 CenterY=-69.424 CenterZ=0 NormalX=0 NormalY=0 NormalZ=1 AngleXU=0 Radius=1
    g333: BSplineCurve PolesCount=3 KnotsCount=2 Degree=2 IsPeriodic=0
    g334: GeomPoint X=42.5666 Y=-67.3492 Z=0
    g335: GeomPoint X=46.0728 Y=-69.424 Z=0
    g336: Circle CenterX=46.0728 CenterY=-87.7794 CenterZ=0 NormalX=0 NormalY=0 NormalZ=1 AngleXU=0 Radius=1
    g337: Circle CenterX=46.0728 CenterY=-91.7794 CenterZ=0 NormalX=0 NormalY=0 NormalZ=1 AngleXU=0 Radius=1
    g338: Circle CenterX=42.0728 CenterY=-91.7794 CenterZ=0 NormalX=0 NormalY=0 NormalZ=1 AngleXU=0 Radius=1
    g339: BSplineCurve PolesCount=3 KnotsCount=2 Degree=2 IsPeriodic=0
    g340: GeomPoint X=46.0728 Y=-87.7794 Z=0
    g341: GeomPoint X=42.0728 Y=-91.7794 Z=0
    g342: Circle CenterX=2.07281 CenterY=-91.7794 CenterZ=0 NormalX=0 NormalY=0 NormalZ=1 AngleXU=0 Radius=1
    g343: Circle CenterX=-1.92719 CenterY=-91.7794 CenterZ=0 NormalX=0 NormalY=0 NormalZ=1 AngleXU=0 Radius=1
    g344: Circle CenterX=1.57905 CenterY=-89.8542 CenterZ=0 NormalX=0 NormalY=0 NormalZ=1 AngleXU=0 Radius=1
    g345: BSplineCurve PolesCount=3 KnotsCount=2 Degree=2 IsPeriodic=0
    g346: GeomPoint X=2.07281 Y=-91.7794 Z=0
    g347: GeomPoint X=1.57905 Y=-89.8542 Z=0
  constraints (574):
    c: Coincident(g0,g2)
    c: Block(g0)
    c: Block(g1)
    c: Vertical(g3)
    c: Vertical(g4)
    c: Block(g4)
    c: Block(g3)
    c: Tangent(g5,g8) = 1.5708
    c: Tangent(g5,g7) = -1.5708
    c: Tangent(g7,g6) = -1.5708
    c: Tangent(g8,g6) = 1.5708
    c: Vertical(g7)
    c: Equal(g5,g6)
    c: Block(g8)
    c: Block(g7)
    c: Tangent(g9,g10) = 1.5708
    c: Tangent(g10,g12) = 1.5708
    c: Equal(g9,g12)
    c: Coincident(g11,g9)
    c: Coincident(g11,g12)
    c: Block(g10)
    c: Block(g11)
    c: Weight(g13) = 1
    c: Equal(g13,g14)
    c: Equal(g13,g15)
    c: InternalAlignment(g13,g16)
    c: InternalAlignment(g14,g16)
    c: InternalAlignment(g15,g16)
    c: InternalAlignment(g17,g16)
    c: InternalAlignment(g18,g16)
    c: Weight(g19) = 1
    c: Equal(g19,g20)
    c: Equal(g19,g21)
    c: InternalAlignment(g19,g22)
    c: InternalAlignment(g20,g22)
    c: InternalAlignment(g21,g22)
    c: InternalAlignment(g23,g22)
    c: InternalAlignment(g24,g22)
    c: Block(g22)
    c: Block(g16)
    c: Weight(g25) = 1
    c: Equal(g25,g26)
    c: Equal(g25,g27)
    c: InternalAlignment(g25,g28)
    c: InternalAlignment(g26,g28)
    c: InternalAlignment(g27,g28)
    c: InternalAlignment(g29,g28)
    c: InternalAlignment(g30,g28)
    c: Weight(g31) = 1
    c: Equal(g31,g32)
    c: Equal(g31,g33)
    c: InternalAlignment(g31,g34)
    c: InternalAlignment(g32,g34)
    c: InternalAlignment(g33,g34)
    c: InternalAlignment(g35,g34)
    c: InternalAlignment(g36,g34)
    c: Block(g34)
    c: Block(g28)
    c: Weight(g37) = 1
    c: Equal(g37,g38)
    c: Equal(g37,g39)
    c: InternalAlignment(g37,g40)
    c: InternalAlignment(g38,g40)
    c: InternalAlignment(g39,g40)
    c: InternalAlignment(g41,g40)
    c: InternalAlignment(g42,g40)
    c: Weight(g43) = 1
    c: Equal(g43,g44)
    c: Equal(g43,g45)
    c: InternalAlignment(g43,g46)
    c: InternalAlignment(g44,g46)
    c: InternalAlignment(g45,g46)
    c: InternalAlignment(g47,g46)
    c: InternalAlignment(g48,g46)
    c: Block(g40)
    c: Block(g46)
    c: Coincident(g49,g4)
    c: Coincident(g49,g3)
    c: Horizontal(g49)
    c: Distance(g49) = 450
    c: Coincident(g50,g4)
    c: Coincident(g50,g3)
    c: Horizontal(g50)
    c: Horizontal(g51)
    c: Coincident(g2,g51)
    c: Block(g51)
    c: Coincident(g1,g51)
    c: Weight(g52) = 1
    c: Equal(g52,g53)
    c: Equal(g52,g54)
    c: InternalAlignment(g52,g55)
    c: InternalAlignment(g53,g55)
    c: InternalAlignment(g54,g55)
    c: InternalAlignment(g56,g55)
    c: InternalAlignment(g57,g55)
    c: Block(g55)
    c: Weight(g58) = 1
    c: Equal(g58,g59)
    c: Equal(g58,g60)
    c: InternalAlignment(g58,g61)
    c: InternalAlignment(g59,g61)
    c: InternalAlignment(g60,g61)
    c: InternalAlignment(g62,g61)
    c: InternalAlignment(g63,g61)
    c: Block(g61)
    c: Weight(g64) = 1
    c: Equal(g64,g65)
    c: Equal(g64,g66)
    c: InternalAlignment(g64,g67)
    c: InternalAlignment(g65,g67)
    c: InternalAlignment(g66,g67)
    c: InternalAlignment(g68,g67)
    c: InternalAlignment(g69,g67)
    c: Block(g67)
    c: Weight(g70) = 1
    c: Equal(g70,g71)
    c: Equal(g70,g72)
    c: InternalAlignment(g70,g73)
    c: InternalAlignment(g71,g73)
    c: InternalAlignment(g72,g73)
    c: InternalAlignment(g74,g73)
    c: InternalAlignment(g75,g73)
    c: Block(g73)
    c: Weight(g76) = 1
    c: Equal(g76,g77)
    c: Equal(g76,g78)
    c: InternalAlignment(g76,g79)
    c: InternalAlignment(g77,g79)
    c: InternalAlignment(g78,g79)
    c: InternalAlignment(g80,g79)
    c: InternalAlignment(g81,g79)
    c: Weight(g82) = 1
    c: Equal(g82,g83)
    c: Equal(g82,g84)
    c: InternalAlignment(g82,g85)
    c: InternalAlignment(g83,g85)
    c: InternalAlignment(g84,g85)
    c: InternalAlignment(g86,g85)
    c: InternalAlignment(g87,g85)
    c: Block(g79)
    c: Block(g85)
    c: Coincident(g88,g79)
    c: Coincident(g88,g85)
    c: Vertical(g88)
    c: Coincident(g89,g79)
    c: Coincident(g89,g61)
    c: Coincident(g90,g61)
    c: Coincident(g90,g85)
    c: Weight(g91) = 1
    c: Equal(g91,g92)
    c: Equal(g91,g93)
    c: InternalAlignment(g91,g94)
    c: InternalAlignment(g92,g94)
    c: InternalAlignment(g93,g94)
    c: InternalAlignment(g95,g94)
    c: InternalAlignment(g96,g94)
    c: Weight(g97) = 1
    c: Equal(g97,g98)
    c: Equal(g97,g99)
    c: InternalAlignment(g97,g100)
    c: InternalAlignment(g98,g100)
    c: InternalAlignment(g99,g100)
    c: InternalAlignment(g101,g100)
    c: InternalAlignment(g102,g100)
    c: Block(g94)
    c: Block(g100)
    c: Coincident(g103,g94)
    c: Coincident(g103,g100)
    c: Vertical(g103)
    c: Coincident(g104,g94)
    c: Coincident(g104,g55)
    c: Coincident(g105,g55)
    c: Coincident(g105,g100)
    c: Weight(g106) = 1
    c: Equal(g106,g107)
    c: Equal(g106,g108)
    c: InternalAlignment(g106,g109)
    c: InternalAlignment(g107,g109)
    c: InternalAlignment(g108,g109)
    c: InternalAlignment(g110,g109)
    c: InternalAlignment(g111,g109)
    c: Weight(g112) = 1
    c: Equal(g112,g113)
    c: Equal(g112,g114)
    c: InternalAlignment(g112,g115)
    c: InternalAlignment(g113,g115)
    c: InternalAlignment(g114,g115)
    c: InternalAlignment(g116,g115)
    c: InternalAlignment(g117,g115)
    c: Block(g109)
    c: Block(g115)
    c: Coincident(g118,g109)
    c: Coincident(g118,g115)
    c: Vertical(g118)
    c: Coincident(g119,g115)
    c: Coincident(g119,g73)
    c: Coincident(g120,g73)
    c: Coincident(g120,g109)
    c: Weight(g121) = 1
    c: Equal(g121,g122)
    c: Equal(g121,g123)
    c: InternalAlignment(g121,g124)
    c: InternalAlignment(g122,g124)
    c: InternalAlignment(g123,g124)
    c: InternalAlignment(g125,g124)
    c: InternalAlignment(g126,g124)
    c: Weight(g127) = 1
    c: Equal(g127,g128)
    c: Equal(g127,g129)
    c: InternalAlignment(g127,g130)
    c: InternalAlignment(g128,g130)
    c: InternalAlignment(g129,g130)
    c: InternalAlignment(g131,g130)
    c: InternalAlignment(g132,g130)
    c: Block(g124)
    c: Block(g130)
    c: Coincident(g133,g124)
    c: Coincident(g133,g130)
    c: Vertical(g133)
    c: Coincident(g134,g130)
    c: Coincident(g134,g67)
    c: Coincident(g135,g67)
    c: Coincident(g135,g124)
    c: Weight(g136) = 1
    c: Equal(g136,g137)
    c: Equal(g136,g138)
    c: InternalAlignment(g136,g139)
    c: InternalAlignment(g137,g139)
    c: InternalAlignment(g138,g139)
    c: InternalAlignment(g140,g139)
    c: InternalAlignment(g141,g139)
    c: Weight(g142) = 1
    c: Equal(g142,g143)
    c: Equal(g142,g144)
    c: InternalAlignment(g142,g145)
    c: InternalAlignment(g143,g145)
    c: InternalAlignment(g144,g145)
    c: InternalAlignment(g146,g145)
    c: InternalAlignment(g147,g145)
    c: Weight(g148) = 1
    c: Equal(g148,g149)
    c: Equal(g148,g150)
    c: InternalAlignment(g148,g151)
    c: InternalAlignment(g149,g151)
    c: InternalAlignment(g150,g151)
    c: InternalAlignment(g152,g151)
    c: InternalAlignment(g153,g151)
    c: Weight(g154) = 1
    c: Equal(g154,g155)
    c: Equal(g154,g156)
    c: InternalAlignment(g154,g157)
    c: InternalAlignment(g155,g157)
    c: InternalAlignment(g156,g157)
    c: InternalAlignment(g158,g157)
    c: InternalAlignment(g159,g157)
    c: Block(g157)
    c: Block(g151)
    c: Block(g145)
    c: Block(g139)
    c: Coincident(g160,g34)
    c: Coincident(g160,g157)
    c: Coincident(g161,g157)
    c: Coincident(g161,g151)
    c: Horizontal(g161)
    c: Coincident(g162,g151)
    c: Coincident(g162,g34)
    c: Vertical(g162)
    c: Coincident(g163,g28)
    c: Coincident(g163,g145)
    c: Vertical(g163)
    c: Coincident(g164,g145)
    c: Coincident(g164,g139)
    c: Horizontal(g164)
    c: Coincident(g165,g139)
    c: Coincident(g165,g28)
    c: Weight(g166) = 1
    c: Equal(g166,g167)
    c: Equal(g166,g168)
    c: InternalAlignment(g166,g169)
    c: InternalAlignment(g167,g169)
    c: InternalAlignment(g168,g169)
    c: InternalAlignment(g170,g169)
    c: InternalAlignment(g171,g169)
    c: Weight(g172) = 1
    c: Equal(g172,g173)
    c: Equal(g172,g174)
    c: InternalAlignment(g172,g175)
    c: InternalAlignment(g173,g175)
    c: InternalAlignment(g174,g175)
    c: InternalAlignment(g176,g175)
    c: InternalAlignment(g177,g175)
    c: Weight(g178) = 1
    c: Equal(g178,g179)
    c: Equal(g178,g180)
    c: InternalAlignment(g178,g181)
    c: InternalAlignment(g179,g181)
    c: InternalAlignment(g180,g181)
    c: InternalAlignment(g182,g181)
    c: InternalAlignment(g183,g181)
    c: Weight(g184) = 1
    c: Equal(g184,g185)
    c: Equal(g184,g186)
    c: InternalAlignment(g184,g187)
    c: InternalAlignment(g185,g187)
    c: InternalAlignment(g186,g187)
    c: InternalAlignment(g188,g187)
    c: InternalAlignment(g189,g187)
    c: Block(g187)
    c: Block(g181)
    c: Block(g175)
    c: Block(g169)
    c: Coincident(g190,g187)
    c: Coincident(g190,g181)
    c: Horizontal(g190)
    c: Coincident(g191,g181)
    c: Coincident(g191,g16)
    c: Vertical(g191)
    c: Coincident(g192,g22)
    c: Coincident(g192,g175)
    c: Vertical(g192)
    c: Coincident(g193,g175)
    c: Coincident(g193,g169)
    c: Horizontal(g193)
    c: Coincident(g194,g169)
    c: Coincident(g194,g22)
    c: Coincident(g195,g16)
    c: Weight(g196) = 1
    c: Equal(g196,g197)
    c: Equal(g196,g198)
    c: InternalAlignment(g196,g199)
    c: InternalAlignment(g197,g199)
    c: InternalAlignment(g198,g199)
    c: InternalAlignment(g200,g199)
    c: InternalAlignment(g201,g199)
    c: Weight(g202) = 1
    c: Equal(g202,g203)
    c: Equal(g202,g204)
    c: InternalAlignment(g202,g205)
    c: InternalAlignment(g203,g205)
    c: InternalAlignment(g204,g205)
    c: InternalAlignment(g206,g205)
    c: InternalAlignment(g207,g205)
    c: Block(g205)
    c: Block(g199)
    c: Coincident(g208,g205)
    c: Coincident(g208,g40)
    c: Coincident(g209,g40)
    c: Coincident(g209,g199)
    c: Coincident(g210,g199)
    c: Coincident(g210,g205)
    c: Vertical(g210)
    c: Weight(g211) = 1
    c: Equal(g211,g212)
    c: Equal(g211,g213)
    c: InternalAlignment(g211,g214)
    c: InternalAlignment(g212,g214)
    c: InternalAlignment(g213,g214)
    c: InternalAlignment(g215,g214)
    c: InternalAlignment(g216,g214)
    c: Weight(g217) = 1
    c: Equal(g217,g218)
    c: Equal(g217,g219)
    c: InternalAlignment(g217,g220)
    c: InternalAlignment(g218,g220)
    c: InternalAlignment(g219,g220)
    c: InternalAlignment(g221,g220)
    c: InternalAlignment(g222,g220)
    c: Block(g220)
    c: Block(g214)
    c: Coincident(g223,g214)
    c: Coincident(g223,g46)
    c: Coincident(g224,g46)
    c: Coincident(g224,g220)
    c: Coincident(g225,g220)
    c: Coincident(g225,g214)
    c: Vertical(g225)
    c: Horizontal(g226)
    c: Block(g226)
    c: Vertical(g227)
    c: Block(g227)
    c: Block(g228)
    c: Weight(g229) = 1
    c: Equal(g229,g230)
    c: Equal(g229,g231)
    c: InternalAlignment(g229,g232)
    c: InternalAlignment(g230,g232)
    c: InternalAlignment(g231,g232)
    c: InternalAlignment(g233,g232)
    c: InternalAlignment(g234,g232)
    c: Weight(g235) = 1
    c: Equal(g235,g236)
    c: Equal(g235,g237)
    c: InternalAlignment(g235,g238)
    c: InternalAlignment(g236,g238)
    c: InternalAlignment(g237,g238)
    c: InternalAlignment(g239,g238)
    c: InternalAlignment(g240,g238)
    c: Weight(g241) = 1
    c: Equal(g241,g242)
    c: Equal(g241,g243)
    c: InternalAlignment(g241,g244)
    c: InternalAlignment(g242,g244)
    c: InternalAlignment(g243,g244)
    c: InternalAlignment(g245,g244)
    c: InternalAlignment(g246,g244)
    c: Weight(g247) = 1
    c: Equal(g247,g248)
    c: Equal(g247,g249)
    c: InternalAlignment(g247,g250)
    c: InternalAlignment(g248,g250)
    c: InternalAlignment(g249,g250)
    c: InternalAlignment(g251,g250)
    c: InternalAlignment(g252,g250)
    c: Block(g232)
    c: Block(g238)
    c: Block(g244)
    c: Block(g250)
    c: Coincident(g253,g238)
    c: Coincident(g253,g232)
    c: Horizontal(g253)
    c: Block(g195)
    c: Weight(g254) = 1
    c: Equal(g254,g255)
    c: Equal(g254,g256)
    c: InternalAlignment(g254,g257)
    c: InternalAlignment(g255,g257)
    c: InternalAlignment(g256,g257)
    c: InternalAlignment(g258,g257)
    c: InternalAlignment(g259,g257)
    c: Weight(g260) = 1
    c: Equal(g260,g261)
    c: Equal(g260,g262)
    c: InternalAlignment(g260,g263)
    c: InternalAlignment(g261,g263)
    c: InternalAlignment(g262,g263)
    c: InternalAlignment(g264,g263)
    c: InternalAlignment(g265,g263)
    c: Weight(g266) = 1
    c: Equal(g266,g267)
    c: Equal(g266,g268)
    c: InternalAlignment(g266,g269)
    c: InternalAlignment(g267,g269)
    c: InternalAlignment(g268,g269)
    c: InternalAlignment(g270,g269)
    c: InternalAlignment(g271,g269)
    c: Weight(g272) = 1
    c: Equal(g272,g273)
    c: Equal(g272,g274)
    c: InternalAlignment(g272,g275)
    c: InternalAlignment(g273,g275)
    c: InternalAlignment(g274,g275)
    c: InternalAlignment(g276,g275)
    c: InternalAlignment(g277,g275)
    c: Block(g257)
    c: Block(g263)
    c: Block(g269)
    c: Block(g275)
    c: Coincident(g278,g269)
    c: Coincident(g278,g275)
    c: Horizontal(g278)
    c: Coincident(g279,g275)
    c: Coincident(g279,g257)
    c: Vertical(g279)
    c: Coincident(g280,g257)
    c: Coincident(g280,g263)
    c: Coincident(g281,g263)
    c: Coincident(g281,g269)
    c: Vertical(g281)
    c: Weight(g282) = 1
    c: Equal(g282,g283)
    c: Equal(g282,g284)
    c: InternalAlignment(g282,g285)
    c: InternalAlignment(g283,g285)
    c: InternalAlignment(g284,g285)
    c: InternalAlignment(g286,g285)
    c: InternalAlignment(g287,g285)
    c: Weight(g288) = 1
    c: Equal(g288,g289)
    c: Equal(g288,g290)
    c: InternalAlignment(g288,g291)
    c: InternalAlignment(g289,g291)
    c: InternalAlignment(g290,g291)
    c: InternalAlignment(g292,g291)
    c: InternalAlignment(g293,g291)
    c: Weight(g294) = 1
    c: Equal(g294,g295)
    c: Equal(g294,g296)
    c: InternalAlignment(g294,g297)
    c: InternalAlignment(g295,g297)
    c: InternalAlignment(g296,g297)
    c: InternalAlignment(g298,g297)
    c: InternalAlignment(g299,g297)
    c: Block(g297)
    c: Block(g291)
    c: Block(g285)
    c: Coincident(g300,g291)
    c: Coincident(g300,g285)
    c: Coincident(g301,g285)
    c: Coincident(g301,g297)
    c: Vertical(g301)
    c: Coincident(g302,g297)
    c: Coincident(g302,g291)
    c: Horizontal(g302)
    c: Weight(g303) = 1
    c: Equal(g303,g304)
    c: InternalAlignment(g303,g305)
    c: InternalAlignment(g304,g305)
    c: InternalAlignment(g306,g305)
    c: InternalAlignment(g307,g305)
    c: Weight(g308) = 1
    c: Equal(g308,g309)
    c: Equal(g308,g310)
    c: InternalAlignment(g308,g311)
    c: InternalAlignment(g309,g311)
    c: InternalAlignment(g310,g311)
    c: InternalAlignment(g312,g311)
    c: InternalAlignment(g313,g311)
    c: Weight(g314) = 1
    c: Equal(g314,g315)
    c: Equal(g314,g316)
    c: InternalAlignment(g314,g317)
    c: InternalAlignment(g315,g317)
    c: InternalAlignment(g316,g317)
    c: InternalAlignment(g318,g317)
    c: InternalAlignment(g319,g317)
    c: Equal(g320,g321)
    c: Equal(g320,g322)
    c: InternalAlignment(g320,g323)
    c: InternalAlignment(g321,g323)
    c: InternalAlignment(g322,g323)
    c: InternalAlignment(g324,g323)
    c: InternalAlignment(g325,g323)
    c: Block(g311)
    c: Block(g317)
    c: Block(g323)
    c: Block(g305)
    c: Coincident(g326,g305)
    c: Coincident(g326,g311)
    c: Horizontal(g326)
    c: Coincident(g327,g311)
    c: Coincident(g327,g317)
    c: Vertical(g327)
    c: Coincident(g328,g317)
    c: Coincident(g328,g323)
    c: Horizontal(g328)
    c: Coincident(g329,g323)
    c: Coincident(g329,g305)
    c: Weight(g330) = 1
    c: Equal(g330,g331)
    c: Equal(g330,g332)
    c: InternalAlignment(g330,g333)
    c: InternalAlignment(g331,g333)
    c: InternalAlignment(g332,g333)
    c: InternalAlignment(g334,g333)
    c: InternalAlignment(g335,g333)
    c: Weight(g336) = 1
    c: Equal(g336,g337)
    c: Equal(g336,g338)
    c: InternalAlignment(g336,g339)
    c: InternalAlignment(g337,g339)
    c: InternalAlignment(g338,g339)
    c: InternalAlignment(g340,g339)
    c: InternalAlignment(g341,g339)
    c: Weight(g342) = 1
    c: Equal(g342,g343)
    c: Equal(g342,g344)
    c: InternalAlignment(g342,g345)
    c: InternalAlignment(g343,g345)
    c: InternalAlignment(g344,g345)
    c: InternalAlignment(g346,g345)
    c: InternalAlignment(g347,g345)
    c: Block(g345)
    c: Block(g339)
    c: Block(g333)
FEATURE [Sketcher::SketchObject] Sketch001
  FullyConstrained = true
  MapMode = 4
  Placement = pos=(0,0,0) rot=(0.57735,0.57735,0.57735;2.0944rad)
  Support = -> [Sketch]
  sketch-geometry (46):
    g0: BSplineCurve PolesCount=3 KnotsCount=2 Degree=2 IsPeriodic=0
    g1: ArcOfCircle CenterX=73.1223 CenterY=-32.291 CenterZ=0 NormalX=0 NormalY=0 NormalZ=1 AngleXU=0 Radius=13 StartAngle=5.92268 EndAngle=9.06428
    g2: ArcOfCircle CenterX=66.7816 CenterY=-49.1439 CenterZ=0 NormalX=0 NormalY=0 NormalZ=1 AngleXU=0 Radius=13 StartAngle=2.78068 EndAngle=5.92131
    g3: ArcOfCircle CenterX=55.9263 CenterY=-78.1807 CenterZ=0 NormalX=0 NormalY=0 NormalZ=1 AngleXU=0 Radius=13 StartAngle=5.92268 EndAngle=9.06428
    g4: ArcOfCircle CenterX=49.5884 CenterY=-95.0342 CenterZ=0 NormalX=0 NormalY=0 NormalZ=1 AngleXU=0 Radius=13 StartAngle=2.78068 EndAngle=5.92131
    g5: ArcOfCircle CenterX=38.7206 CenterY=-124.067 CenterZ=0 NormalX=0 NormalY=0 NormalZ=1 AngleXU=0 Radius=13 StartAngle=5.92268 EndAngle=9.06428
    g6: ArcOfCircle CenterX=32.3875 CenterY=-140.92 CenterZ=0 NormalX=0 NormalY=0 NormalZ=1 AngleXU=0 Radius=13 StartAngle=2.78068 EndAngle=5.92131
    g7: ArcOfCircle CenterX=21.4715 CenterY=-169.934 CenterZ=0 NormalX=0 NormalY=0 NormalZ=1 AngleXU=0 Radius=13 StartAngle=5.92268 EndAngle=9.06428
    g8: ArcOfCircle CenterX=15.1336 CenterY=-186.787 CenterZ=0 NormalX=0 NormalY=0 NormalZ=1 AngleXU=0 Radius=13 StartAngle=2.78068 EndAngle=5.92131
    g9-g12: Circle x4 (B-spline internal-alignment scaffolding for g13; pole/knot coordinates omitted)
    g13: BSplineCurve PolesCount=4 KnotsCount=2 Degree=3 IsPeriodic=0
    g14: GeomPoint X=28.8094 Y=-19.0875 Z=0
    g15: GeomPoint X=47.0443 Y=-50.4712 Z=0
    g16: Circle CenterX=53.5586 CenterY=-23.2695 CenterZ=0 NormalX=0 NormalY=0 NormalZ=1 AngleXU=0 Radius=3.24518
    g17: Circle CenterX=-195.441 CenterY=-127.082 CenterZ=0 NormalX=0 NormalY=0 NormalZ=1 AngleXU=0 Radius=1
    g18: Circle CenterX=-8.24091 CenterY=-197.481 CenterZ=0 NormalX=0 NormalY=0 NormalZ=1 AngleXU=0 Radius=1
    g19: Circle CenterX=12.8789 CenterY=-141.321 CenterZ=0 NormalX=0 NormalY=0 NormalZ=1 AngleXU=0 Radius=1
    g20: BSplineCurve PolesCount=3 KnotsCount=2 Degree=2 IsPeriodic=0
    g21: GeomPoint X=-195.441 Y=-127.082 Z=0
    g22: GeomPoint X=12.8789 Y=-141.321 Z=0
    g23: Circle CenterX=-12.8016 CenterY=-179.036 CenterZ=0 NormalX=0 NormalY=0 NormalZ=1 AngleXU=0 Radius=10.5072
    g24: Circle CenterX=0.933922 CenterY=-166.43 CenterZ=0 NormalX=0 NormalY=0 NormalZ=1 AngleXU=0 Radius=3.26661
    g25: Circle CenterX=-33.5518 CenterY=-176.44 CenterZ=0 NormalX=0 NormalY=0 NormalZ=1 AngleXU=0 Radius=5.64388
    g26: Circle CenterX=-47.2366 CenterY=-173.859 CenterZ=0 NormalX=0 NormalY=0 NormalZ=1 AngleXU=0 Radius=3.01653
    g27: Circle CenterX=-56.2595 CenterY=-171.456 CenterZ=0 NormalX=0 NormalY=0 NormalZ=1 AngleXU=0 Radius=2.12826
    g28: ArcOfCircle CenterX=51.2151 CenterY=-198.473 CenterZ=0 NormalX=0 NormalY=0 NormalZ=1 AngleXU=0 Radius=20 StartAngle=2.78189 EndAngle=4.35269
    g29: LineSegment StartX=32.4951 StartY=-191.433 StartZ=0 EndX=94.6578 EndY=-26.1352 EndZ=0
    g30: LineSegment StartX=43.1192 StartY=-220.001 StartZ=0 EndX=-196.497 EndY=-129.89 EndZ=0
    g31: LineSegment StartX=43.1192 StartY=-220.001 StartZ=0 EndX=44.1752 EndY=-217.193 EndZ=0
    g32: LineSegment StartX=117.223 StartY=-19.0875 StartZ=0 EndX=117.223 EndY=-16.0875 EndZ=0
    g33: LineSegment StartX=117.223 StartY=-16.0875 StartZ=0 EndX=17.2232 EndY=-16.0875 EndZ=0
    g34: LineSegment StartX=17.2232 StartY=-16.0875 StartZ=0 EndX=17.2232 EndY=-19.0875 EndZ=0
    g35: LineSegment StartX=28.8094 StartY=-19.0875 StartZ=0 EndX=17.2232 EndY=-19.0875 EndZ=0
    g36: LineSegment StartX=47.0443 StartY=-50.4712 StartZ=0 EndX=12.8789 EndY=-141.321 EndZ=0
    g37: LineSegment StartX=-195.441 StartY=-127.082 StartZ=0 EndX=-196.497 EndY=-129.89 EndZ=0
    g38: LineSegment StartX=85.2866 StartY=-36.8766 StartZ=0 EndX=78.9396 EndY=-53.7463 EndZ=0
    g39: LineSegment StartX=60.9579 StartY=-27.7053 StartZ=0 EndX=54.6191 EndY=-44.5532 EndZ=0
    g40: LineSegment StartX=68.0907 StartY=-82.7664 StartZ=0 EndX=61.7465 EndY=-99.6365 EndZ=0
    g41: LineSegment StartX=43.7619 StartY=-73.595 StartZ=0 EndX=37.426 EndY=-90.4435 EndZ=0
    g42: LineSegment StartX=50.885 StartY=-128.652 StartZ=0 EndX=44.5456 EndY=-145.522 EndZ=0
    g43: LineSegment StartX=26.5562 StartY=-119.481 StartZ=0 EndX=20.2251 EndY=-136.329 EndZ=0
    g44: LineSegment StartX=9.3071 StartY=-165.349 StartZ=0 EndX=2.97115 EndY=-182.197 EndZ=0
    g45: LineSegment StartX=33.6358 StartY=-174.52 StartZ=0 EndX=27.2917 EndY=-191.39 EndZ=0
  constraints (71):
    c: Block(g0)
    c: Block(g1)
    c: Block(g2)
    c: Block(g4)
    c: Block(g3)
    c: Block(g6)
    c: Block(g5)
    c: Block(g8)
    c: Block(g7)
    c: Weight(g9) = 1
    c: Equal(g9,g10)
    c: Equal(g9,g11)
    c: Equal(g9,g12)
    c: InternalAlignment(g9-g12 -> g13) x4
    c: InternalAlignment(g14,g13)
    c: InternalAlignment(g15,g13)
    c: Block(g16)
    c: Weight(g17) = 1
    c: Equal(g17,g18)
    c: Equal(g17,g19)
    c: InternalAlignment(g17,g20)
    c: InternalAlignment(g18,g20)
    c: InternalAlignment(g19,g20)
    c: InternalAlignment(g21,g20)
    c: InternalAlignment(g22,g20)
    c: Block(g20)
    c: Block(g23)
    c: Block(g24)
    c: Block(g25)
    c: Block(g26)
    c: Block(g27)
    c: Block(g28)
    c: Coincident(g29,g28)
    c: Coincident(g29,g0)
    c: Block(g13)
    c: Coincident(g31,g30)
    c: Coincident(g31,g28)
    c: Block(g31)
    c: Coincident(g32,g0)
    c: Vertical(g32)
    c: Coincident(g33,g32)
    c: Horizontal(g33)
    c: Coincident(g34,g33)
    c: Vertical(g34)
    c: Block(g33)
    c: Coincident(g35,g13)
    c: Coincident(g35,g34)
    c: Horizontal(g35)
    c: Coincident(g36,g13)
    c: Coincident(g36,g20)
    c: Coincident(g37,g20)
    c: Coincident(g37,g30)
    c: Block(g30)
    c: Coincident(g38,g1)
    c: Coincident(g38,g2)
    c: Coincident(g39,g1)
    c: Coincident(g39,g2)
    c: Coincident(g40,g3)
    c: Coincident(g40,g4)
    c: Coincident(g41,g3)
    c: Coincident(g41,g4)
    c: Coincident(g42,g5)
    c: Coincident(g42,g6)
    c: Coincident(g43,g5)
    c: Coincident(g43,g6)
    c: Coincident(g44,g7)
    c: Coincident(g44,g8)
    c: Coincident(g45,g7)
    c: Coincident(g45,g8)
    c: Distance(g30) = 256
    c: Distance(g33) = 100
FEATURE [Part::Extrusion] Extrude002
  Base = -> Sketch001
  Dir = (1,0,0)
  DirMode = 2
  FaceMakerClass = Part::FaceMakerBullseye
  LengthFwd = 8
  LengthRev = 0
  Solid = true
  Symmetric = false
FEATURE [Sketcher::SketchObject] Sketch002
  FullyConstrained = true
  sketch-geometry (20):
    g0: LineSegment StartX=-2.77179 StartY=-200.304 StartZ=0 EndX=5.22821 EndY=-200.304 EndZ=0
    g1: LineSegment StartX=5.22821 StartY=-200.304 StartZ=0 EndX=5.22821 EndY=-197.304 EndZ=0
    g2: LineSegment StartX=-2.77179 StartY=-200.304 StartZ=0 EndX=-2.77179 EndY=-197.304 EndZ=0
    g3: LineSegment StartX=5.22821 StartY=-197.304 StartZ=0 EndX=8.22821 EndY=-197.304 EndZ=0
    g4: LineSegment StartX=-2.77179 StartY=-197.304 StartZ=0 EndX=-5.77179 EndY=-197.304 EndZ=0
    g5: LineSegment StartX=19.2282 StartY=-203.304 StartZ=0 EndX=19.2282 EndY=-206.304 EndZ=0
    g6: LineSegment StartX=-16.7718 StartY=-203.304 StartZ=0 EndX=-16.7718 EndY=-206.304 EndZ=0
    g7: LineSegment StartX=-16.7718 StartY=-206.304 StartZ=0 EndX=19.2282 EndY=-206.304 EndZ=0
    g8: Circle CenterX=-16.7718 CenterY=-203.304 CenterZ=0 NormalX=0 NormalY=0 NormalZ=1 AngleXU=0 Radius=1
    g9: Circle CenterX=-5.77179 CenterY=-203.304 CenterZ=0 NormalX=0 NormalY=0 NormalZ=1 AngleXU=0 Radius=1
    g10: Circle CenterX=-5.77179 CenterY=-197.304 CenterZ=0 NormalX=0 NormalY=0 NormalZ=1 AngleXU=0 Radius=1
    g11: BSplineCurve PolesCount=3 KnotsCount=2 Degree=2 IsPeriodic=0
    g12: GeomPoint X=-16.7718 Y=-203.304 Z=0
    g13: GeomPoint X=-5.77179 Y=-197.304 Z=0
    g14: Circle CenterX=19.2282 CenterY=-203.304 CenterZ=0 NormalX=0 NormalY=0 NormalZ=1 AngleXU=0 Radius=1
    g15: Circle CenterX=8.22821 CenterY=-203.304 CenterZ=0 NormalX=0 NormalY=0 NormalZ=1 AngleXU=0 Radius=1
    g16: Circle CenterX=8.22821 CenterY=-197.304 CenterZ=0 NormalX=0 NormalY=0 NormalZ=1 AngleXU=0 Radius=1
    g17: BSplineCurve PolesCount=3 KnotsCount=2 Degree=2 IsPeriodic=0
    g18: GeomPoint X=19.2282 Y=-203.304 Z=0
    g19: GeomPoint X=8.22821 Y=-197.304 Z=0
  constraints (41):
    c: Horizontal(g0)
    c: Distance(g0) = 8
    c: Coincident(g1,g0)
    c: Vertical(g1)
    c: Distance(g1) = 3
    c: Coincident(g2,g0)
    c: Vertical(g2)
    c: Distance(g2) = 3
    c: Coincident(g3,g1)
    c: Horizontal(g3)
    c: Distance(g3) = 3
    c: Coincident(g4,g2)
    c: Horizontal(g4)
    c: Distance(g4) = 3
    c: Vertical(g5)
    c: Vertical(g6)
    c: Coincident(g7,g6)
    c: Coincident(g7,g5)
    c: Weight(g8) = 1
    c: Equal(g8,g9)
    c: Equal(g8,g10)
    c: Coincident(g11,g4)
    c: InternalAlignment(g8,g11)
    c: InternalAlignment(g9,g11)
    c: InternalAlignment(g10,g11)
    c: InternalAlignment(g12,g11)
    c: InternalAlignment(g13,g11)
    c: Coincident(g17,g5)
    c: Weight(g14) = 1
    c: Equal(g14,g15)
    c: Equal(g14,g16)
    c: Coincident(g17,g3)
    c: InternalAlignment(g14,g17)
    c: InternalAlignment(g15,g17)
    c: InternalAlignment(g16,g17)
    c: InternalAlignment(g18,g17)
    c: InternalAlignment(g19,g17)
    c: Block(g7)
    c: Block(g17)
    c: Block(g11)
    c: Block(g6)
FEATURE [Part::Extrusion] Extrude003
  Base = -> Sketch002
  Dir = (0,0,1)
  DirMode = 2
  FaceMakerClass = Part::FaceMakerBullseye
  LengthFwd = 260
  LengthRev = 0
  Solid = true
  Symmetric = false
FEATURE [Part::Extrusion] Extrude
  Base = -> Sketch
  Dir = (0,0,1)
  DirMode = 2
  FaceMakerClass = Part::FaceMakerBullseye
  LengthFwd = 14
  LengthRev = 0
  Solid = true
  Symmetric = false
